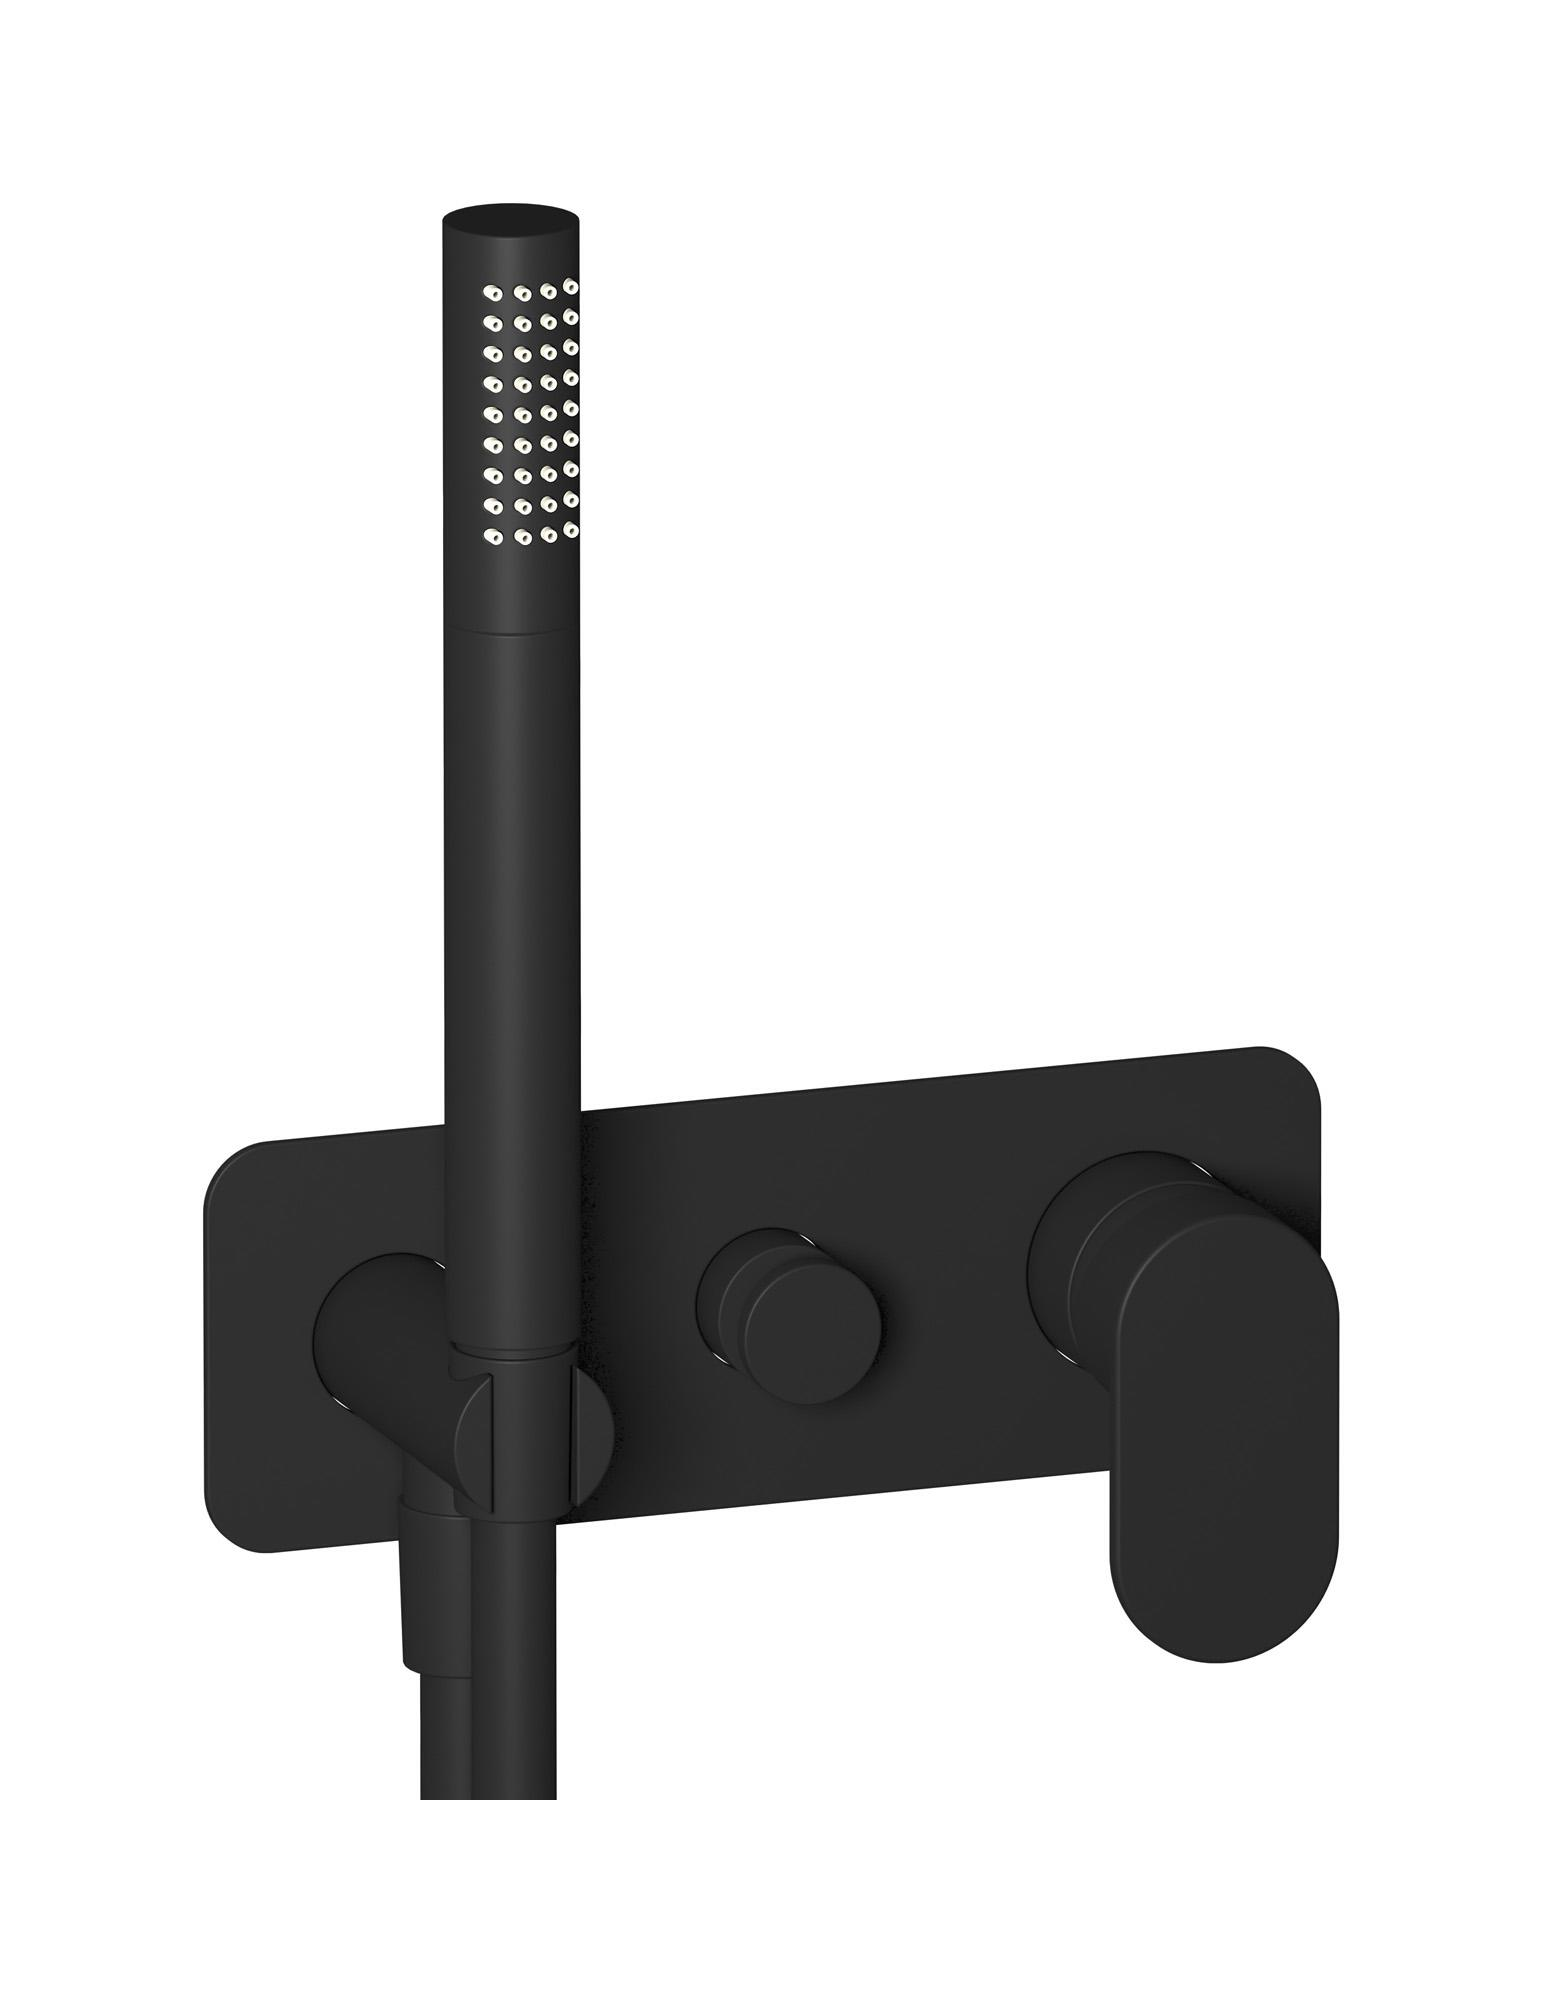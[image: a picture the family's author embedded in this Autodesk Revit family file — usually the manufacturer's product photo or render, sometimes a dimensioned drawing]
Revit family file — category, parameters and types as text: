
# Revit family: K2313
name_source: partatom
category: Apparecchi idraulici
units: mm (PartAtom-declared; Revit-internal decimal feet)

## family parameters
Basato su piano di lavoro = No
Condiviso = No
Mantieni orientamento annotazione = No
Numero OmniClass = 23.45.55.17
Punto di calcolo locali = No
Quota connettore circolare = Usa diametro
Sempre verticale = Sì
Taglio con vuoti quando caricato = No
Tipo di parte = Normale
Titolo OmniClass = Mixing Faucets

## types (9) — shared parameters
Cold water inlet = 10 mm  [stored 0.0328084 ft]
Commenti sul tipo = Wall mixer
Connessione CW = No
Connessione HW = No
Connessione di scarico = No
Connessione di ventilazione = No
Descrizione = Exposed parts for manual wall mixer with two ways diverter and shower kit
Hot water inlet = 10 mm  [stored 0.0328084 ft]
Produttore = IB Rubinetterie S.p.A.
URL = https://www.weareib.it
zero-valued in all types: Prospetto di default

## per-type parameters (varying)
| type | Finishes surface | Immagine tipo | Modello |
| Chrome | IB_Chrome | K2313CC.jpg | K2313CC |
| Brushed nickel | IB_Brushed nickel | K2313SS.jpg | K2313SS |
| Matt black | IB_matt black | K2313NP.jpg | K2313NP |
| Matt white | IB_matt white | K2313BO.jpg | K2313BO |
| Platinum | IB_Platinum | K2313PL.jpg | K2313PL |
| Pale gold | IB_Pale gold | K2313II.jpg | K2313II |
| Brushed pale gold | IB_brushed pale gold | K2313IS.jpg | K2313IS |
| Rose gold | IB_Rose gold | K2313RS.jpg | K2313RS |
| Gold | IB_gold | K2313OO.jpg | K2313OO |

note: [stored X ft] marks values corroborated as IEEE doubles in the binary element streams (Revit-internal decimal feet)
